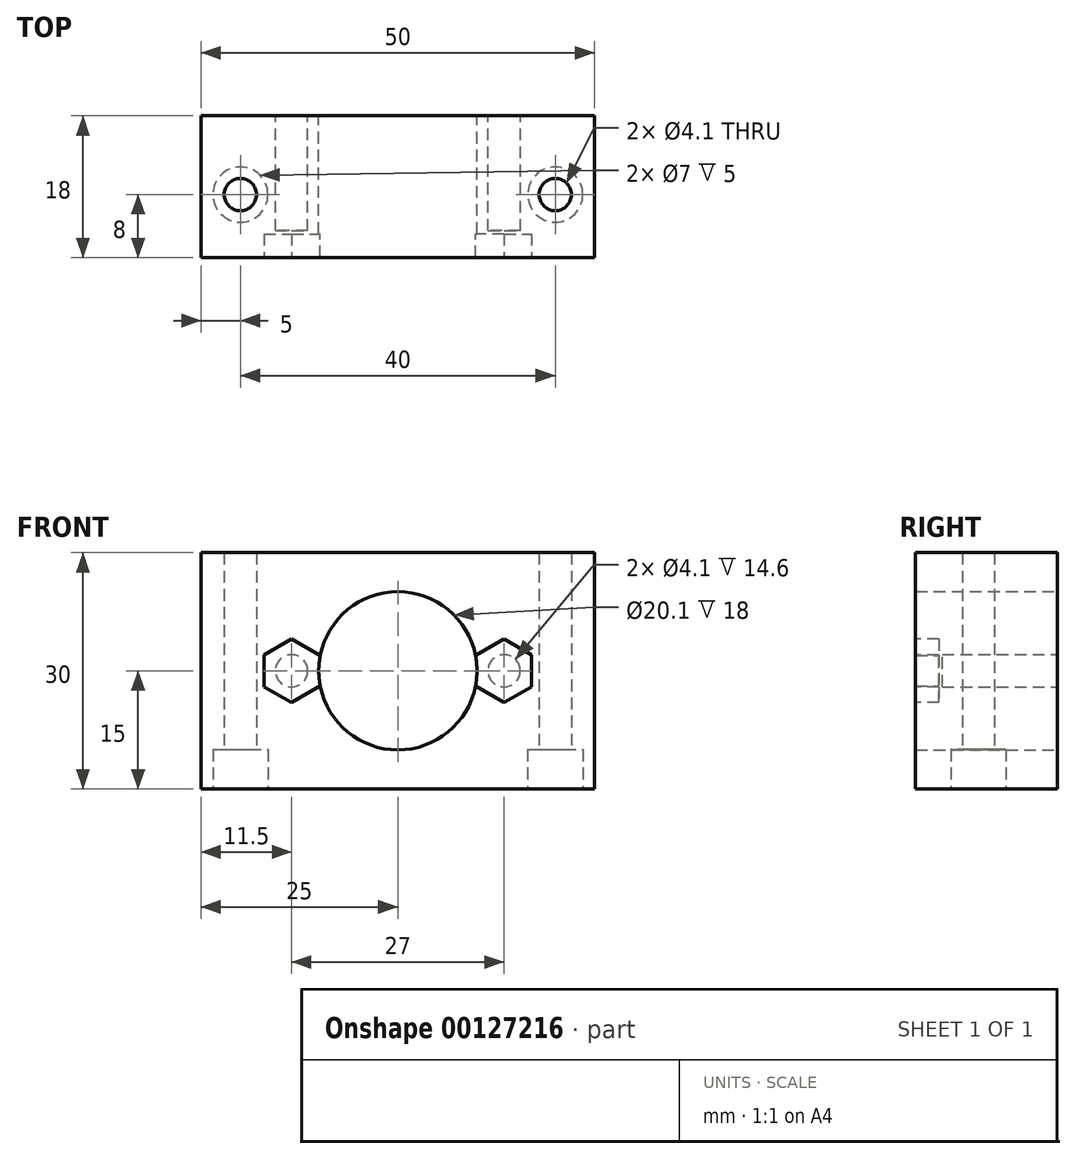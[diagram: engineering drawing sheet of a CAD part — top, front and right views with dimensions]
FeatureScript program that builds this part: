
annotation { "Feature Type Name" : "Feature", "Feature Type Description" : "" }
export const myFeature = defineFeature(function(context is Context, id is Id, definition is map)
    precondition{}
    {
        {
            var Q0;
            Q0=qCreatedBy(makeId("Front.planeOp"),FACE);
            var sketch = newSketch(context, id + "F0", { "sketchPlane" : qUnion([Q0])});
            skCircle(sketch, "E0", {"center": v(0, 0) * mm, "radius": 10.05 * mm});
            skLineSegment(sketch, "E1", {"start": v(0, 0) * mm, "end": v(0, 15) * mm});
            skLineSegment(sketch, "E2", {"start": v(0, 0) * mm, "end": v(0, -15) * mm});
            skLineSegment(sketch, "E3", {"start": v(-25, 0) * mm, "end": v(-25, -15) * mm});
            skLineSegment(sketch, "E4", {"start": v(-25, -15) * mm, "end": v(0, -15) * mm});
            skLineSegment(sketch, "E5", {"start": v(-25, 0) * mm, "end": v(-25, 15) * mm});
            skLineSegment(sketch, "E6", {"start": v(-25, 15) * mm, "end": v(0, 15) * mm});
            skLineSegment(sketch, "E7", {"start": v(0, -15) * mm, "end": v(25, -15) * mm});
            skLineSegment(sketch, "E8", {"start": v(25, -15) * mm, "end": v(25, 0) * mm});
            skLineSegment(sketch, "E9", {"start": v(25, 0) * mm, "end": v(25, 15) * mm});
            skLineSegment(sketch, "E10", {"start": v(25, 15) * mm, "end": v(0, 15) * mm});
            skLineSegment(sketch, "E11", {"start": v(0, 0) * mm, "end": v(-13.5, 0) * mm});
            skLineSegment(sketch, "E12", {"start": v(0, 0) * mm, "end": v(13.5, 0) * mm});
            skCircle(sketch, "E13", {"center": v(-13.5, 0) * mm, "radius": 2.05 * mm});
            skCircle(sketch, "E14", {"center": v(13.5, 0) * mm, "radius": 2.05 * mm});
            skSolve(sketch);
        }
        {
            var Q0;
            Q0=qSketchRegion(id+"F0",true);
            extrude(context, id + "F1", {"entities" : qUnion([Q0]), "depth" : 18 * mm});
        }
        {
            var Q0;
            Q0=makeQuery(id+"F1.opExtrude","SWEPT_FACE",FACE,{"disambiguationData":[OSD([sQuery(id+"F0.wireOp",EDGE,"E4"),sQuery(id+"F0.wireOp",EDGE,"E7")])]});
            var sketch = newSketch(context, id + "F2", { "sketchPlane" : qUnion([Q0])});
            skLineSegment(sketch, "E15", {"start": v(25, 0) * mm, "end": v(25, 10) * mm});
            skLineSegment(sketch, "E16", {"start": v(-25, 0) * mm, "end": v(-25, 10) * mm});
            skLineSegment(sketch, "E17", {"start": v(25, 10) * mm, "end": v(15, 10) * mm});
            skLineSegment(sketch, "E18", {"start": v(-25, 10) * mm, "end": v(-15, 10) * mm});
            skCircle(sketch, "E19", {"center": v(20, 10) * mm, "radius": 2.05 * mm});
            skCircle(sketch, "E20", {"center": v(-20, 10) * mm, "radius": 2.05 * mm});
            skSolve(sketch);
        }
        {
            var Q0;
            Q0=qSketchRegion(id+"F2",true);
            extrude(context, id + "F3", {"entities" : qUnion([Q0]), "operationType" : NewBodyOperationType.REMOVE, "oppositeDirection" : true, "depth" : 30 * mm});
        }
        {
            var Q0;
            Q0=makeQuery(id+"F1.opExtrude","SWEPT_FACE",FACE,{"disambiguationData":[OSD([sQuery(id+"F0.wireOp",EDGE,"E4"),sQuery(id+"F0.wireOp",EDGE,"E7")])]});
            var sketch = newSketch(context, id + "F4", { "sketchPlane" : qUnion([Q0])});
            skCircle(sketch, "E21", {"center": v(20, 10) * mm, "radius": 3.5 * mm});
            skCircle(sketch, "E22", {"center": v(-20, 10) * mm, "radius": 3.5 * mm});
            skSolve(sketch);
        }
        {
            var Q0;
            Q0=qSketchRegion(id+"F4",true);
            extrude(context, id + "F5", {"entities" : qUnion([Q0]), "operationType" : NewBodyOperationType.REMOVE, "oppositeDirection" : true, "depth" : 5 * mm});
        }
        {
            var Q0;
            Q0=makeQuery(id+"F1.opExtrude","CAP_FACE",FACE,{"disambiguationData":[OSD([sQuery(id+"F0.wireOp",EDGE,"E0"),sQuery(id+"F0.wireOp",EDGE,"E3"),sQuery(id+"F0.wireOp",EDGE,"E4"),sQuery(id+"F0.wireOp",EDGE,"E5"),sQuery(id+"F0.wireOp",EDGE,"E6"),sQuery(id+"F0.wireOp",EDGE,"E7"),sQuery(id+"F0.wireOp",EDGE,"E8"),sQuery(id+"F0.wireOp",EDGE,"E9"),sQuery(id+"F0.wireOp",EDGE,"E10"),sQuery(id+"F0.wireOp",EDGE,"E13"),sQuery(id+"F0.wireOp",EDGE,"E14")])],"isStart":false});
            var sketch = newSketch(context, id + "F6", { "sketchPlane" : qUnion([Q0])});
            skLineSegment(sketch, "E23", {"start": v(-13.5, 0) * mm, "end": v(-13.5, -4.05) * mm});
            skLineSegment(sketch, "E24", {"start": v(-13.5, 0) * mm, "end": v(-13.5, 4.05) * mm});
            skCircle(sketch, "E25.cCircle", {"center": v(-13.5, 0) * mm, "radius": 4.05 * mm, "construction": true});
            skLineSegment(sketch, "E25.0", {"start": v(-13.5, 4.05) * mm, "end": v(-10, 2.02) * mm});
            skLineSegment(sketch, "E25.2", {"start": v(-10, -2.02) * mm, "end": v(-13.5, -4.05) * mm});
            skLineSegment(sketch, "E25.3", {"start": v(-13.5, -4.05) * mm, "end": v(-17, -2.03) * mm});
            skLineSegment(sketch, "E25.4", {"start": v(-17, -2.03) * mm, "end": v(-17, 2.02) * mm});
            skLineSegment(sketch, "E25.5", {"start": v(-17, 2.02) * mm, "end": v(-13.5, 4.05) * mm});
            skLineSegment(sketch, "E26", {"start": v(-10, 2.02) * mm, "end": v(-7.8, 0.75) * mm});
            skLineSegment(sketch, "E27", {"start": v(-10, -2.02) * mm, "end": v(-7.97, -0.86) * mm});
            skLineSegment(sketch, "E28", {"start": v(-7.97, -0.86) * mm, "end": v(-7.8, 0.75) * mm});
            skLineSegment(sketch, "E29", {"start": v(13.5, 0) * mm, "end": v(13.5, 4.05) * mm});
            skLineSegment(sketch, "E30", {"start": v(13.5, 0) * mm, "end": v(13.5, -4.05) * mm});
            skCircle(sketch, "E31.cCircle", {"center": v(13.5, 0) * mm, "radius": 4.05 * mm, "construction": true});
            skLineSegment(sketch, "E31.0", {"start": v(13.5, 4.05) * mm, "end": v(17, 2.02) * mm});
            skLineSegment(sketch, "E31.1", {"start": v(17, 2.03) * mm, "end": v(17, -2.02) * mm});
            skLineSegment(sketch, "E31.2", {"start": v(17, -2.02) * mm, "end": v(13.5, -4.05) * mm});
            skLineSegment(sketch, "E31.3", {"start": v(13.5, -4.05) * mm, "end": v(10, -2.03) * mm});
            skLineSegment(sketch, "E31.4", {"start": v(10, -2.03) * mm, "end": v(10, 2.02) * mm});
            skLineSegment(sketch, "E31.5", {"start": v(10, 2.02) * mm, "end": v(13.5, 4.05) * mm});
            skLineSegment(sketch, "E32", {"start": v(10, 2.02) * mm, "end": v(7.5, 0.58) * mm});
            skLineSegment(sketch, "E33", {"start": v(10, -2.03) * mm, "end": v(7.26, -0.44) * mm});
            skLineSegment(sketch, "E34", {"start": v(7.26, -0.44) * mm, "end": v(7.5, 0.58) * mm});
            skSolve(sketch);
        }
        {
            var Q0;
            Q0=qSketchRegion(id+"F6",true);
            extrude(context, id + "F7", {"entities" : qUnion([Q0]), "operationType" : NewBodyOperationType.REMOVE, "oppositeDirection" : true, "depth" : 3 * mm});
        }
        {
            var Q0;
            Q0=makeQuery(id+"F7.boolean.opBoolean","COPY",FACE,{"derivedFrom":makeQuery(id+"F7.opExtrude","CAP_FACE",FACE,{"disambiguationData":[OSD([sQuery(id+"F6.wireOp",EDGE,"E31.0"),sQuery(id+"F6.wireOp",EDGE,"E31.1"),sQuery(id+"F6.wireOp",EDGE,"E31.2"),sQuery(id+"F6.wireOp",EDGE,"E31.3"),sQuery(id+"F6.wireOp",EDGE,"E31.5"),sQuery(id+"F6.wireOp",EDGE,"E32"),sQuery(id+"F6.wireOp",EDGE,"E33"),sQuery(id+"F6.wireOp",EDGE,"E34")])],"isStart":false})});
            var sketch = newSketch(context, id + "F8", { "sketchPlane" : qUnion([Q0])});
            skCircle(sketch, "E35", {"center": v(13.5, 0) * mm, "radius": 2.05 * mm});
            skSolve(sketch);
        }
        {
            var Q0;
            Q0=makeQuery(id+"F7.boolean.opBoolean","COPY",FACE,{"derivedFrom":makeQuery(id+"F7.opExtrude","CAP_FACE",FACE,{"disambiguationData":[OSD([sQuery(id+"F6.wireOp",EDGE,"E25.0"),sQuery(id+"F6.wireOp",EDGE,"E25.2"),sQuery(id+"F6.wireOp",EDGE,"E25.3"),sQuery(id+"F6.wireOp",EDGE,"E25.4"),sQuery(id+"F6.wireOp",EDGE,"E25.5"),sQuery(id+"F6.wireOp",EDGE,"E26"),sQuery(id+"F6.wireOp",EDGE,"E27"),sQuery(id+"F6.wireOp",EDGE,"E28")])],"isStart":false})});
            var sketch = newSketch(context, id + "F9", { "sketchPlane" : qUnion([Q0])});
            skCircle(sketch, "E36", {"center": v(-13.5, 0) * mm, "radius": 2.05 * mm});
            skSolve(sketch);
        }
        {
            var Q0;
            Q0=qSketchRegion(id+"F8",true);
            var Q1;
            Q1=qSketchRegion(id+"F9",true);
            extrude(context, id + "F10", {"entities" : qUnion([Q0, Q1]), "operationType" : NewBodyOperationType.ADD, "oppositeDirection" : true, "depth" : 0.4 * mm});
        }
    });
